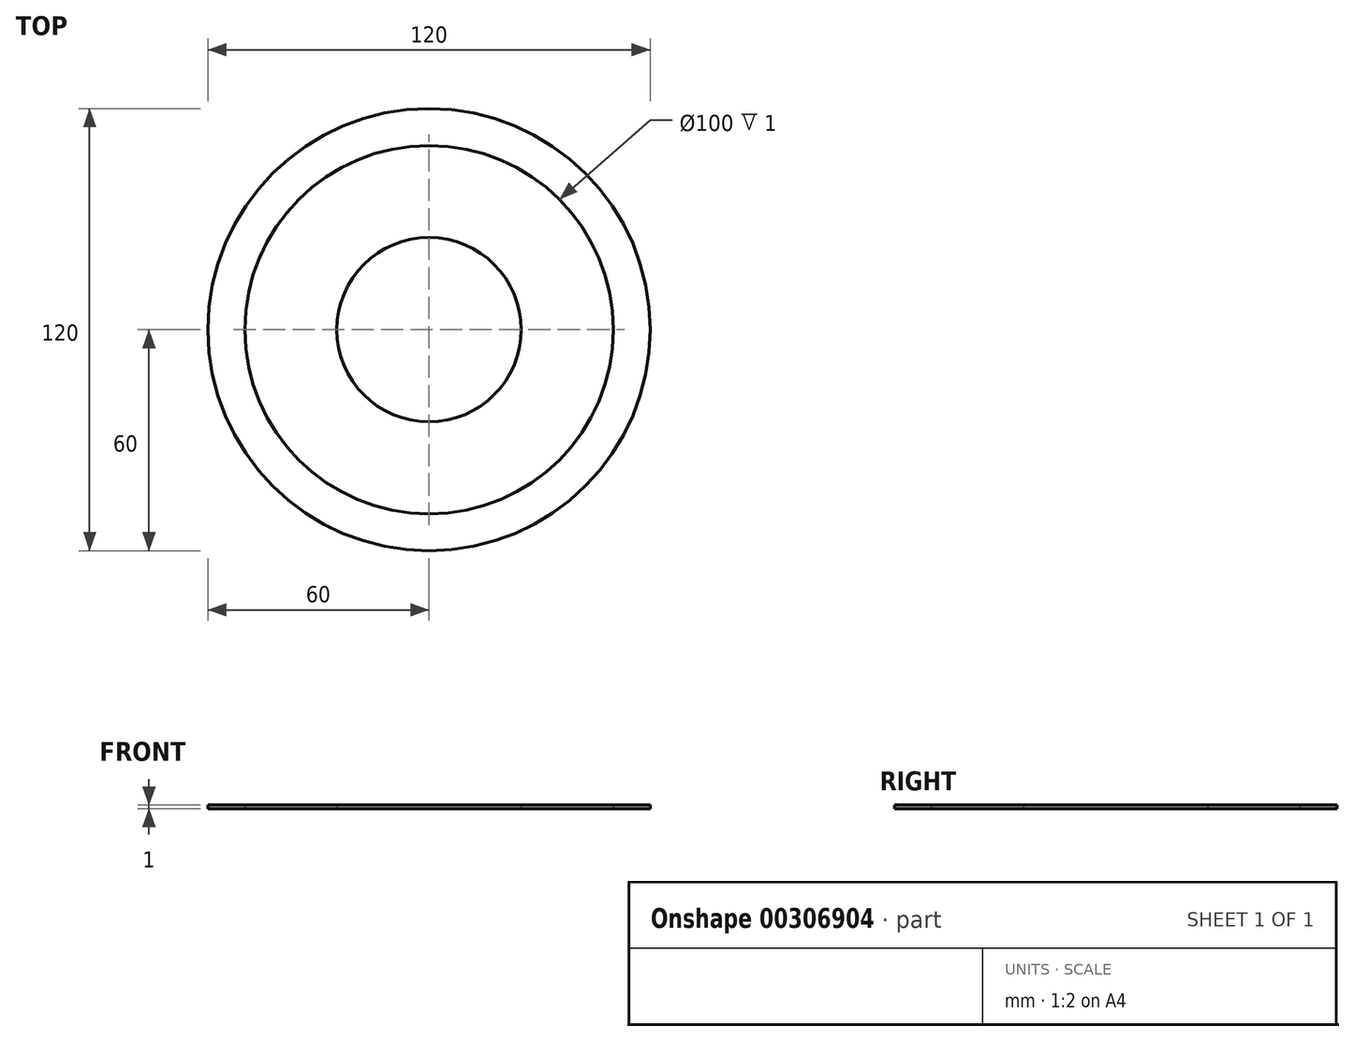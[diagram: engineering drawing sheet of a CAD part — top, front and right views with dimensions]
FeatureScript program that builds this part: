
annotation { "Feature Type Name" : "Feature", "Feature Type Description" : "" }
export const myFeature = defineFeature(function(context is Context, id is Id, definition is map)
    precondition{}
    {
        {
            var Q0;
            Q0=qCreatedBy(makeId("Top.planeOp"),FACE);
            var sketch = newSketch(context, id + "F0", { "sketchPlane" : qUnion([Q0])});
            skCircle(sketch, "E0", {"center": v(0, 0) * mm, "radius": 60 * mm});
            skCircle(sketch, "E1", {"center": v(0, 0) * mm, "radius": 25 * mm});
            skCircle(sketch, "E2", {"center": v(0, 0) * mm, "radius": 50 * mm});
            skSolve(sketch);
        }
        {
            var Q0;
            Q0=makeQuery(id+"F0.imprint","IMPRINT",FACE,{"disambiguationData":[TD([[makeQuery(id+"F0.imprint","IMPRINT",EDGE,{"derivedFrom":sQuery(id+"F0.wireOp",EDGE,"E0")}),1.0]])]});
            var Q1;
            Q1=makeQuery(id+"F0.imprint","IMPRINT",FACE,{"disambiguationData":[TD([[makeQuery(id+"F0.imprint","IMPRINT",EDGE,{"derivedFrom":sQuery(id+"F0.wireOp",EDGE,"E1")}),1.0]])]});
            var Q2;
            Q2 = qSketchRegion(id + "F0", true);
            extrude(context, id + "F1", {"entities" : qUnion([Q0, Q1, Q2]), "depth" : 1 * mm});
        }
    });
